# Revit family: Bathtub-Freestanding-American_Standard-Studio-2549004
name_source: partatom
category: Plumbing Fixtures
revit_build: Autodesk Revit 2016 (Build: 20150714_1515(x64)
units: mm (PartAtom-declared; Revit-internal decimal feet)

## family parameters
Always vertical = No
Cut with Voids When Loaded = No
OmniClass Number = 23.45.05.14.21
OmniClass Title = Bathtubs
Part Type = Normal
Room Calculation Point = No
Round Connector Dimension = Use Diameter
Shared = Yes
Work Plane-Based = Yes

## types (1)
- 2549004
    Assembly Code = D2010510
    CW Connection = Yes
    CWFU = 3
    Default Elevation = 0"
    Description = American Standard 2549004 Studio® S Freestanding Tub
    Finish = Acrylic-American Standard-020-High Gloss White
    GAL. TO OVERFLOW = 68 Gal. (257L)
    HW Connection = Yes
    HWFU = 3
    Height = 24 1/2"
    Installation Type = Floor Mount
    Length = 68"
    Manufacturer = American Standard
    Material = Acrylic-American Standard-020-High Gloss White
    Model = 2549004
    Price = Prices may vary. Please consult Manufacturer Representative for most up-to-date price list.
    URL = https://www.americanstandard-us.com
    Vent Connection = No
    WFU = 4
    Warranty Information = Limited Lifetime warranty
    Waste Connection = Yes
    Waste Connection Diameter = 2 1/8"
    Weight = 145 Lbs. (66 Kg.)  w/WATER : (710 Lbs. (322 Kg.))
    Width = 34"

## geometry (parser evidence)
native form markers: Sweep x2
no freeform markers — native parametric forms only
